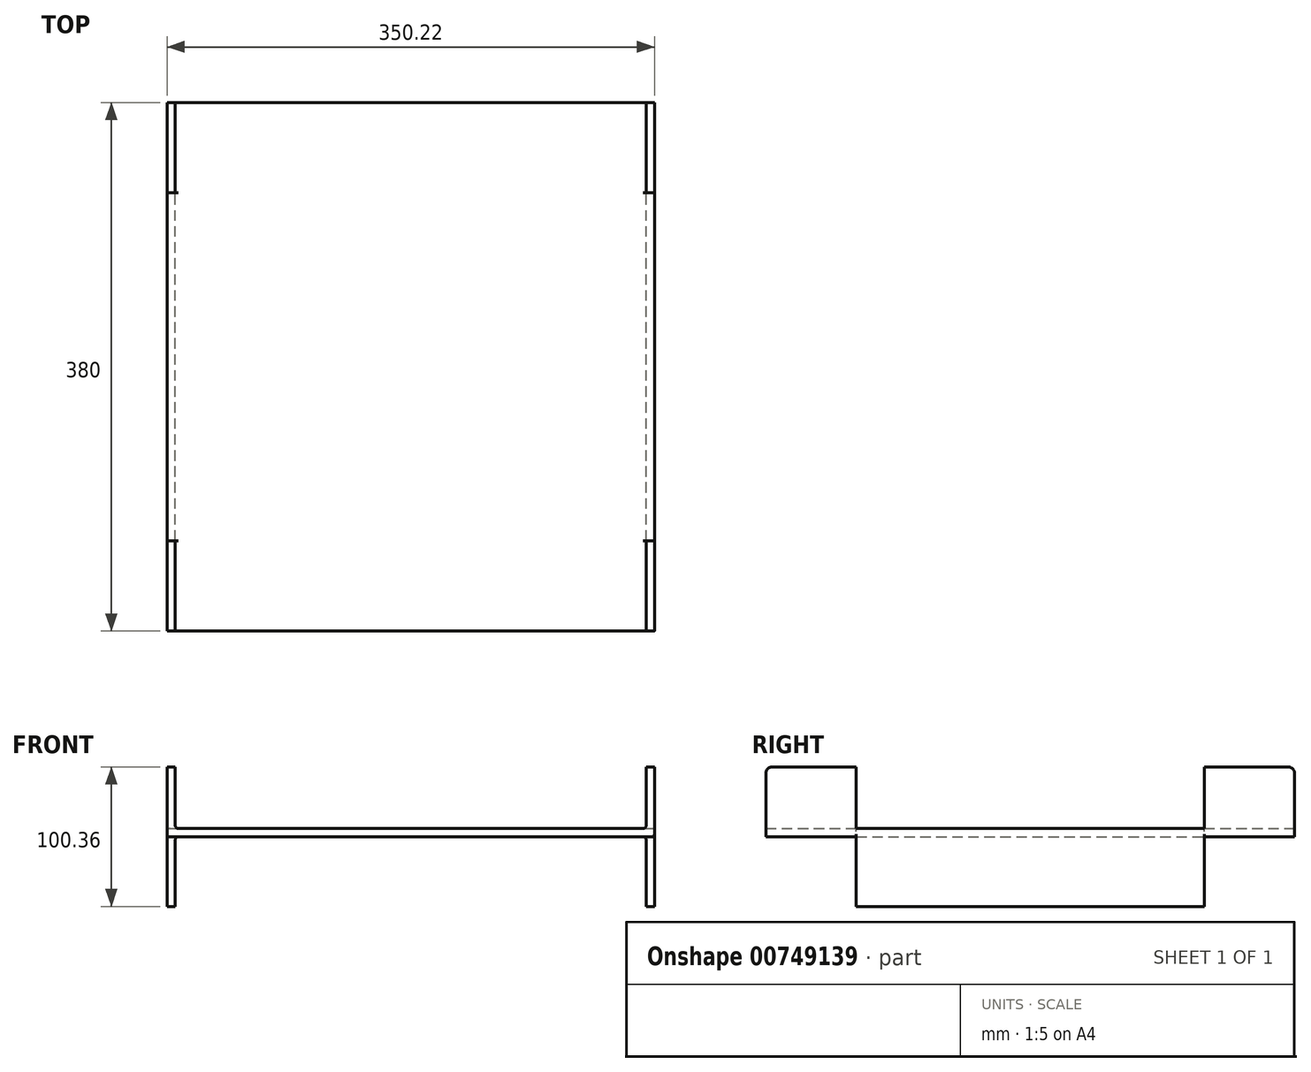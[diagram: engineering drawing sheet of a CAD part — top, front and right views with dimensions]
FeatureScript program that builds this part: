
annotation { "Feature Type Name" : "Feature", "Feature Type Description" : "" }
export const myFeature = defineFeature(function(context is Context, id is Id, definition is map)
    precondition{}
    {
        {
            var Q0;
            Q0=qCreatedBy(makeId("Front.planeOp"),FACE);
            var sketch = newSketch(context, id + "F0", { "sketchPlane" : qUnion([Q0])});
            skLineSegment(sketch, "E0", {"start": v(0, 0) * mm, "end": v(169.11, 0) * mm});
            skLineSegment(sketch, "E1", {"start": v(175.11, 0) * mm, "end": v(175.11, -56) * mm});
            skLineSegment(sketch, "E2.0", {"start": v(169.11, -6) * mm, "end": v(169.11, -56) * mm});
            skLineSegment(sketch, "E2.1", {"start": v(0, -6) * mm, "end": v(169.11, -6) * mm});
            skLineSegment(sketch, "E3", {"start": v(169.11, -56) * mm, "end": v(175.11, -56) * mm});
            skLineSegment(sketch, "E4.MirrorCS", {"start": v(-169.11, -56) * mm, "end": v(-175.11, -56) * mm});
            skLineSegment(sketch, "E5.MirrorCS", {"start": v(0, 0) * mm, "end": v(-175.11, 0) * mm});
            skLineSegment(sketch, "E6.MirrorCS", {"start": v(-175.11, 0) * mm, "end": v(-175.11, -56) * mm});
            skLineSegment(sketch, "E7.MirrorCS", {"start": v(-169.11, -6) * mm, "end": v(-169.11, -56) * mm});
            skLineSegment(sketch, "E8.MirrorCS", {"start": v(0, -6) * mm, "end": v(-169.11, -6) * mm});
            skLineSegment(sketch, "E9", {"start": v(169.11, 0) * mm, "end": v(169.11, 44.36) * mm});
            skLineSegment(sketch, "E10", {"start": v(169.11, 44.36) * mm, "end": v(175.11, 44.36) * mm});
            skLineSegment(sketch, "E11", {"start": v(175.11, 44.36) * mm, "end": v(175.11, 0) * mm});
            skLineSegment(sketch, "E12.MirrorCS", {"start": v(-175.11, 44.36) * mm, "end": v(-175.11, 0) * mm});
            skLineSegment(sketch, "E13.MirrorCS", {"start": v(-169.11, 44.36) * mm, "end": v(-175.11, 44.36) * mm});
            skLineSegment(sketch, "E14.MirrorCS", {"start": v(-169.11, 0) * mm, "end": v(-169.11, 44.36) * mm});
            skSolve(sketch);
        }
        {
            var Q0;
            Q0=makeQuery(id+"F0.imprint","IMPRINT",FACE,{"disambiguationData":[TD([[makeQuery(id+"F0.imprint","IMPRINT",EDGE,{"derivedFrom":sQuery(id+"F0.wireOp",EDGE,"E0")}),-1.0]])]});
            var Q1;
            {var subQ0=sQuery(id+"F0.wireOp",EDGE,"E12.MirrorCS");Q1=makeQuery(id+"F0.imprint","IMPRINT",FACE,{"disambiguationData":[TD([[makeQuery(id+"F0.imprint","IMPRINT",EDGE,{"derivedFrom":subQ0}),1.0]])]});}
            extrude(context, id + "F1", {"entities" : qUnion([Q0, Q1]), "depth" : 380 * mm, "offsetDistance" : 25 * mm, "symmetric" : true});
        }
        {
            var Q0;
            Q0=makeQuery(id+"F1.opExtrude","SWEPT_FACE",FACE,{"disambiguationData":[OSD([sQuery(id+"F0.wireOp",EDGE,"E1"),sQuery(id+"F0.wireOp",EDGE,"E11")])]});
            var sketch = newSketch(context, id + "F2", { "sketchPlane" : qUnion([Q0])});
            skLineSegment(sketch, "E15.bottom", {"start": v(0, 0) * mm, "end": v(-125, 0) * mm});
            skLineSegment(sketch, "E15.right", {"start": v(-125, 0) * mm, "end": v(-125, 134.37) * mm});
            skLineSegment(sketch, "E16.MirrorCS", {"start": v(125, 0) * mm, "end": v(125, 134.37) * mm});
            skLineSegment(sketch, "E17.MirrorCS", {"start": v(0, 0) * mm, "end": v(125, 0) * mm});
            skPoint(sketch, "E18.orphan", {"position": v(-190, -6) * mm});
            skPoint(sketch, "E19.orphan", {"position": v(190, -6) * mm});
            skLineSegment(sketch, "E20", {"start": v(-125, 134.37) * mm, "end": v(125, 134.37) * mm});
            skSolve(sketch);
        }
        {
            var Q0;
            {var subQ0=sQuery(id+"F2.wireOp",EDGE,"E17.MirrorCS");Q0=makeQuery(id+"F2.imprint","IMPRINT",FACE,{"disambiguationData":[TD([[makeQuery(id+"F2.imprint","IMPRINT",EDGE,{"derivedFrom":subQ0}),1.0]])]});}
            var Q1;
            {var subQ0=sQuery(id+"F2.wireOp",EDGE,"E15.bottom");Q1=makeQuery(id+"F2.imprint","IMPRINT",FACE,{"disambiguationData":[TD([[makeQuery(id+"F2.imprint","IMPRINT",EDGE,{"derivedFrom":subQ0}),-1.0]])]});}
            extrude(context, id + "F3", {"entities" : qUnion([Q0, Q1]), "operationType" : NewBodyOperationType.REMOVE, "oppositeDirection" : true, "depth" : 500 * mm, "offsetDistance" : 25 * mm});
        }
        {
            var Q0;
            Q0=makeQuery(id+"F1.opExtrude","SWEPT_FACE",FACE,{"disambiguationData":[OSD([sQuery(id+"F0.wireOp",EDGE,"E6.MirrorCS"),sQuery(id+"F0.wireOp",EDGE,"E12.MirrorCS")])]});
            var sketch = newSketch(context, id + "F4", { "sketchPlane" : qUnion([Q0])});
            skLineSegment(sketch, "E21.0", {"start": v(190, -6) * mm, "end": v(125, -6) * mm});
            skLineSegment(sketch, "E22.0", {"start": v(-190, -6) * mm, "end": v(-190, -56) * mm});
            skLineSegment(sketch, "E23.0", {"start": v(190, -6) * mm, "end": v(190, -56) * mm});
            skLineSegment(sketch, "E24.0", {"start": v(190, -56) * mm, "end": v(125, -56) * mm});
            skLineSegment(sketch, "E25", {"start": v(-125, -6) * mm, "end": v(-125, -56) * mm});
            skLineSegment(sketch, "E26", {"start": v(125, -6) * mm, "end": v(125, -56) * mm});
            skPoint(sketch, "E27.orphan", {"position": v(190, 44.36) * mm});
            skLineSegment(sketch, "E28.trimOffspring", {"start": v(-125, -6) * mm, "end": v(-190, -6) * mm});
            skLineSegment(sketch, "E29.trimOffspring", {"start": v(-125, -56) * mm, "end": v(-190, -56) * mm});
            skPoint(sketch, "E30.orphan", {"position": v(-190, 44.36) * mm});
            skSolve(sketch);
        }
        {
            var Q0;
            Q0=makeQuery(id+"F4.imprint","IMPRINT",FACE,{"disambiguationData":[TD([[makeQuery(id+"F4.imprint","IMPRINT",EDGE,{"derivedFrom":sQuery(id+"F4.wireOp",EDGE,"E22.0")}),1.0]])]});
            var Q1;
            Q1=makeQuery(id+"F4.imprint","IMPRINT",FACE,{"disambiguationData":[TD([[makeQuery(id+"F4.imprint","IMPRINT",EDGE,{"derivedFrom":sQuery(id+"F4.wireOp",EDGE,"E21.0")}),1.0]])]});
            extrude(context, id + "F5", {"entities" : qUnion([Q0, Q1]), "operationType" : NewBodyOperationType.REMOVE, "oppositeDirection" : true, "depth" : 500 * mm, "offsetDistance" : 25 * mm});
        }
        {
            var Q0;
            {var subQ1=sQuery(id+"F0.wireOp",EDGE,"E0");var subQ2=sQuery(id+"F0.wireOp",EDGE,"E9");Q0=makeQuery(id+"F3.boolean.opBoolean","SPLIT",EDGE,{"disambiguationData":[TD([makeQuery(id+"F3.opExtrude","SWEPT_FACE",FACE,{"disambiguationData":[OSD([sQuery(id+"F2.wireOp",EDGE,"E16.MirrorCS")])]})])],"derivedFrom":makeQuery(id+"F1.opExtrude","SWEPT_EDGE",EDGE,{"disambiguationData":[OSD([subQ1,subQ2])]})});}
            var Q1;
            {var subQ0=sQuery(id+"F0.wireOp",EDGE,"E9");var subQ2=sQuery(id+"F0.wireOp",EDGE,"E0");Q1=makeQuery(id+"F3.boolean.opBoolean","SPLIT",EDGE,{"disambiguationData":[TD([makeQuery(id+"F3.opExtrude","SWEPT_FACE",FACE,{"disambiguationData":[OSD([sQuery(id+"F2.wireOp",EDGE,"E15.right")])]})])],"derivedFrom":makeQuery(id+"F1.opExtrude","SWEPT_EDGE",EDGE,{"disambiguationData":[OSD([subQ2,subQ0])]})});}
            var Q2;
            Q2=makeQuery(id+"F3.boolean.opBoolean","COPY",EDGE,{"derivedFrom":makeQuery(id+"F3.opExtrude","CAP_EDGE",EDGE,{"disambiguationData":[OSD([sQuery(id+"F2.wireOp",EDGE,"E15.bottom"),sQuery(id+"F2.wireOp",EDGE,"E17.MirrorCS")])],"isStart":true})});
            var Q3;
            Q3=makeQuery(id+"F1.opExtrude","SWEPT_EDGE",EDGE,{"disambiguationData":[OSD([sQuery(id+"F0.wireOp",EDGE,"E2.0"),sQuery(id+"F0.wireOp",EDGE,"E2.1")])]});
            var Q4;
            Q4=makeQuery(id+"F5.boolean.opBoolean","INTERSECT",EDGE,{"derivedFrom":[makeQuery(id+"F1.opExtrude","SWEPT_FACE",FACE,{"disambiguationData":[OSD([sQuery(id+"F0.wireOp",EDGE,"E1"),sQuery(id+"F0.wireOp",EDGE,"E11")])]}),makeQuery(id+"F5.opExtrude","SWEPT_FACE",FACE,{"disambiguationData":[OSD([sQuery(id+"F4.wireOp",EDGE,"E21.0")])]})]});
            var Q5;
            Q5=makeQuery(id+"F5.boolean.opBoolean","INTERSECT",EDGE,{"derivedFrom":[makeQuery(id+"F1.opExtrude","SWEPT_FACE",FACE,{"disambiguationData":[OSD([sQuery(id+"F0.wireOp",EDGE,"E1"),sQuery(id+"F0.wireOp",EDGE,"E11")])]}),makeQuery(id+"F5.opExtrude","SWEPT_FACE",FACE,{"disambiguationData":[OSD([sQuery(id+"F4.wireOp",EDGE,"E28.trimOffspring")])]})]});
            var Q6;
            {var subQ0=sQuery(id+"F0.wireOp",EDGE,"E14.MirrorCS");var subQ1=sQuery(id+"F0.wireOp",EDGE,"E5.MirrorCS");Q6=makeQuery(id+"F3.boolean.opBoolean","SPLIT",EDGE,{"disambiguationData":[TD([makeQuery(id+"F3.opExtrude","SWEPT_FACE",FACE,{"disambiguationData":[OSD([sQuery(id+"F2.wireOp",EDGE,"E16.MirrorCS")])]})])],"derivedFrom":makeQuery(id+"F1.opExtrude","SWEPT_EDGE",EDGE,{"disambiguationData":[OSD([subQ1,subQ0])]})});}
            var Q7;
            {var subQ0=sQuery(id+"F0.wireOp",EDGE,"E14.MirrorCS");var subQ1=sQuery(id+"F0.wireOp",EDGE,"E5.MirrorCS");Q7=makeQuery(id+"F3.boolean.opBoolean","SPLIT",EDGE,{"disambiguationData":[TD([makeQuery(id+"F3.opExtrude","SWEPT_FACE",FACE,{"disambiguationData":[OSD([sQuery(id+"F2.wireOp",EDGE,"E15.right")])]})])],"derivedFrom":makeQuery(id+"F1.opExtrude","SWEPT_EDGE",EDGE,{"disambiguationData":[OSD([subQ1,subQ0])]})});}
            var Q8;
            Q8=makeQuery(id+"F3.boolean.opBoolean","INTERSECT",EDGE,{"derivedFrom":[makeQuery(id+"F1.opExtrude","SWEPT_FACE",FACE,{"disambiguationData":[OSD([sQuery(id+"F0.wireOp",EDGE,"E6.MirrorCS"),sQuery(id+"F0.wireOp",EDGE,"E12.MirrorCS")])]}),makeQuery(id+"F3.opExtrude","SWEPT_FACE",FACE,{"disambiguationData":[OSD([sQuery(id+"F2.wireOp",EDGE,"E15.bottom"),sQuery(id+"F2.wireOp",EDGE,"E17.MirrorCS")])]})]});
            var Q9;
            Q9=makeQuery(id+"F5.boolean.opBoolean","COPY",EDGE,{"derivedFrom":makeQuery(id+"F5.opExtrude","CAP_EDGE",EDGE,{"disambiguationData":[OSD([sQuery(id+"F4.wireOp",EDGE,"E21.0")])],"isStart":true})});
            var Q10;
            Q10=makeQuery(id+"F1.opExtrude","SWEPT_EDGE",EDGE,{"disambiguationData":[OSD([sQuery(id+"F0.wireOp",EDGE,"E7.MirrorCS"),sQuery(id+"F0.wireOp",EDGE,"E8.MirrorCS")])]});
            var Q11;
            Q11=makeQuery(id+"F5.boolean.opBoolean","COPY",EDGE,{"derivedFrom":makeQuery(id+"F5.opExtrude","CAP_EDGE",EDGE,{"disambiguationData":[OSD([sQuery(id+"F4.wireOp",EDGE,"E28.trimOffspring")])],"isStart":true})});
            fillet(context, id + "F6", {"entities" : qUnion([Q0, Q1, Q2, Q3, Q4, Q5, Q6, Q7, Q8, Q9, Q10, Q11]), "radius" : 2 * mm, "tangentPropagation" : true, "allowEdgeOverflow" : false});
        }
        {
            var Q0;
            Q0=makeQuery(id+"F1.opExtrude","CAP_EDGE",EDGE,{"disambiguationData":[OSD([sQuery(id+"F0.wireOp",EDGE,"E10")])],"isStart":false});
            var Q1;
            {var subQ0=sQuery(id+"F0.wireOp",EDGE,"E10");var subQ1=sQuery(id+"F2.wireOp",EDGE,"E15.right");Q1=makeQuery(id+"F3.boolean.opBoolean","COPY",EDGE,{"disambiguationData":[topologyDisambiguationEdgeConnected([makeQuery(id+"F1.opExtrude","SWEPT_FACE",FACE,{"disambiguationData":[OSD([subQ0])]})])],"derivedFrom":makeQuery(id+"F3.opExtrude","SWEPT_EDGE",EDGE,{"disambiguationData":[OSD([subQ0,sQuery(id+"F0.wireOp",EDGE,"E11"),subQ1])]})});}
            var Q2;
            Q2=makeQuery(id+"F1.opExtrude","CAP_EDGE",EDGE,{"disambiguationData":[OSD([sQuery(id+"F0.wireOp",EDGE,"E13.MirrorCS")])],"isStart":false});
            var Q3;
            {var subQ0=sQuery(id+"F2.wireOp",EDGE,"E15.right");Q3=makeQuery(id+"F3.boolean.opBoolean","COPY",EDGE,{"disambiguationData":[topologyDisambiguationEdgeConnected([makeQuery(id+"F1.opExtrude","SWEPT_FACE",FACE,{"disambiguationData":[OSD([sQuery(id+"F0.wireOp",EDGE,"E13.MirrorCS")])]})])],"derivedFrom":makeQuery(id+"F3.opExtrude","SWEPT_EDGE",EDGE,{"disambiguationData":[OSD([sQuery(id+"F0.wireOp",EDGE,"E10"),sQuery(id+"F0.wireOp",EDGE,"E11"),subQ0])]})});}
            var Q4;
            Q4=makeQuery(id+"F1.opExtrude","CAP_EDGE",EDGE,{"disambiguationData":[OSD([sQuery(id+"F0.wireOp",EDGE,"E13.MirrorCS")])],"isStart":true});
            var Q5;
            {var subQ0=sQuery(id+"F2.wireOp",EDGE,"E16.MirrorCS");Q5=makeQuery(id+"F3.boolean.opBoolean","COPY",EDGE,{"disambiguationData":[topologyDisambiguationEdgeConnected([makeQuery(id+"F1.opExtrude","SWEPT_FACE",FACE,{"disambiguationData":[OSD([sQuery(id+"F0.wireOp",EDGE,"E13.MirrorCS")])]})])],"derivedFrom":makeQuery(id+"F3.opExtrude","SWEPT_EDGE",EDGE,{"disambiguationData":[OSD([sQuery(id+"F0.wireOp",EDGE,"E10"),sQuery(id+"F0.wireOp",EDGE,"E11"),subQ0])]})});}
            var Q6;
            {var subQ0=sQuery(id+"F0.wireOp",EDGE,"E10");var subQ1=sQuery(id+"F2.wireOp",EDGE,"E16.MirrorCS");Q6=makeQuery(id+"F3.boolean.opBoolean","COPY",EDGE,{"disambiguationData":[topologyDisambiguationEdgeConnected([makeQuery(id+"F1.opExtrude","SWEPT_FACE",FACE,{"disambiguationData":[OSD([subQ0])]})])],"derivedFrom":makeQuery(id+"F3.opExtrude","SWEPT_EDGE",EDGE,{"disambiguationData":[OSD([subQ0,sQuery(id+"F0.wireOp",EDGE,"E11"),subQ1])]})});}
            var Q7;
            Q7=makeQuery(id+"F1.opExtrude","CAP_EDGE",EDGE,{"disambiguationData":[OSD([sQuery(id+"F0.wireOp",EDGE,"E10")])],"isStart":true});
            var Q8;
            {var subQ0=sQuery(id+"F4.wireOp",EDGE,"E25");Q8=makeQuery(id+"F5.boolean.opBoolean","COPY",EDGE,{"disambiguationData":[topologyDisambiguationEdgeConnected([makeQuery(id+"F1.opExtrude","SWEPT_FACE",FACE,{"disambiguationData":[OSD([sQuery(id+"F0.wireOp",EDGE,"E3")])]})])],"derivedFrom":makeQuery(id+"F5.opExtrude","SWEPT_EDGE",EDGE,{"disambiguationData":[OSD([sQuery(id+"F0.wireOp",EDGE,"E4.MirrorCS"),sQuery(id+"F0.wireOp",EDGE,"E6.MirrorCS"),subQ0,sQuery(id+"F4.wireOp",EDGE,"E29.trimOffspring")])]})});}
            var Q9;
            {var subQ0=sQuery(id+"F4.wireOp",EDGE,"E26");Q9=makeQuery(id+"F5.boolean.opBoolean","COPY",EDGE,{"disambiguationData":[topologyDisambiguationEdgeConnected([makeQuery(id+"F1.opExtrude","SWEPT_FACE",FACE,{"disambiguationData":[OSD([sQuery(id+"F0.wireOp",EDGE,"E3")])]})])],"derivedFrom":makeQuery(id+"F5.opExtrude","SWEPT_EDGE",EDGE,{"disambiguationData":[OSD([sQuery(id+"F0.wireOp",EDGE,"E4.MirrorCS"),sQuery(id+"F0.wireOp",EDGE,"E6.MirrorCS"),sQuery(id+"F4.wireOp",EDGE,"E24.0"),subQ0])]})});}
            var Q10;
            {var subQ0=sQuery(id+"F0.wireOp",EDGE,"E4.MirrorCS");var subQ1=sQuery(id+"F4.wireOp",EDGE,"E26");Q10=makeQuery(id+"F5.boolean.opBoolean","COPY",EDGE,{"disambiguationData":[topologyDisambiguationEdgeConnected([makeQuery(id+"F1.opExtrude","SWEPT_FACE",FACE,{"disambiguationData":[OSD([subQ0])]})])],"derivedFrom":makeQuery(id+"F5.opExtrude","SWEPT_EDGE",EDGE,{"disambiguationData":[OSD([subQ0,sQuery(id+"F0.wireOp",EDGE,"E6.MirrorCS"),sQuery(id+"F4.wireOp",EDGE,"E24.0"),subQ1])]})});}
            var Q11;
            {var subQ0=sQuery(id+"F0.wireOp",EDGE,"E4.MirrorCS");var subQ1=sQuery(id+"F4.wireOp",EDGE,"E25");Q11=makeQuery(id+"F5.boolean.opBoolean","COPY",EDGE,{"disambiguationData":[topologyDisambiguationEdgeConnected([makeQuery(id+"F1.opExtrude","SWEPT_FACE",FACE,{"disambiguationData":[OSD([subQ0])]})])],"derivedFrom":makeQuery(id+"F5.opExtrude","SWEPT_EDGE",EDGE,{"disambiguationData":[OSD([subQ0,sQuery(id+"F0.wireOp",EDGE,"E6.MirrorCS"),subQ1,sQuery(id+"F4.wireOp",EDGE,"E29.trimOffspring")])]})});}
            fillet(context, id + "F7", {"entities" : qUnion([Q0, Q1, Q2, Q3, Q4, Q5, Q6, Q7, Q8, Q9, Q10, Q11]), "radius" : 5 * mm, "tangentPropagation" : true, "allowEdgeOverflow" : false});
        }
    });
